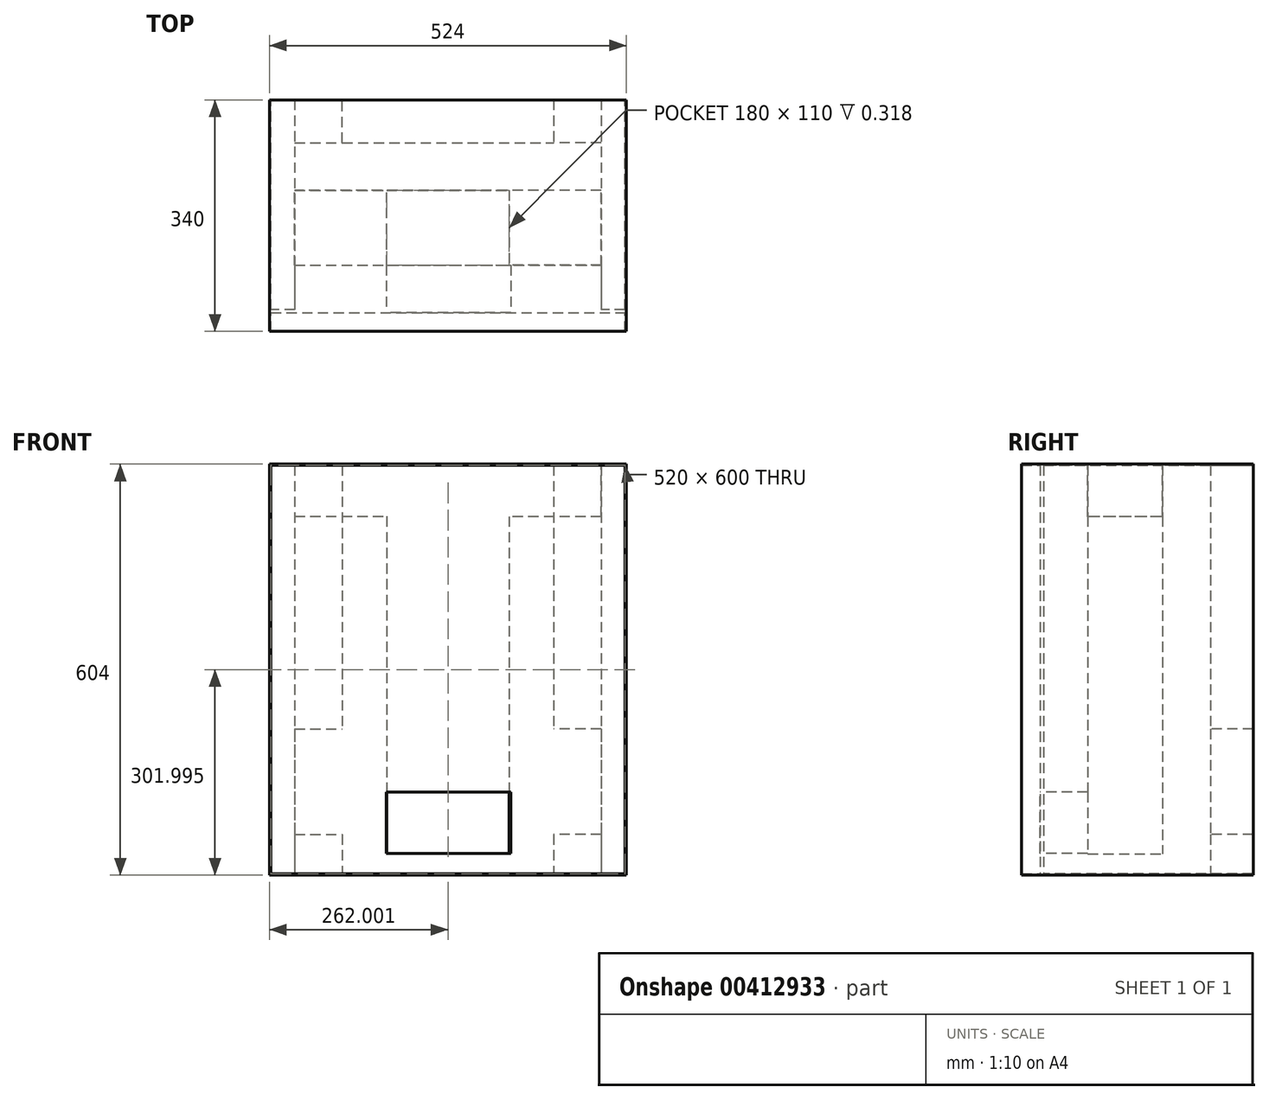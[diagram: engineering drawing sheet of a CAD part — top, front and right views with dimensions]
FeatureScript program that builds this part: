
annotation { "Feature Type Name" : "Feature", "Feature Type Description" : "" }
export const myFeature = defineFeature(function(context is Context, id is Id, definition is map)
    precondition{}
    {
        {
            var Q0;
            Q0=qCreatedBy(makeId("Front.planeOp"),FACE);
            var sketch = newSketch(context, id + "F0", { "sketchPlane" : qUnion([Q0])});
            skLineSegment(sketch, "E0.bottom", {"start": v(-23.65, 566.42) * mm, "end": v(500.35, 566.42) * mm});
            skLineSegment(sketch, "E0.top", {"start": v(-23.65, -37.58) * mm, "end": v(500.35, -37.58) * mm});
            skLineSegment(sketch, "E0.left", {"start": v(-23.65, 566.42) * mm, "end": v(-23.65, -37.58) * mm});
            skLineSegment(sketch, "E0.right", {"start": v(500.35, 566.42) * mm, "end": v(500.35, -37.58) * mm});
            skLineSegment(sketch, "E1.bottom", {"start": v(-21.65, 564.42) * mm, "end": v(498.35, 564.42) * mm});
            skLineSegment(sketch, "E1.top", {"start": v(-21.65, -35.58) * mm, "end": v(498.35, -35.58) * mm});
            skLineSegment(sketch, "E1.left", {"start": v(-21.65, 564.42) * mm, "end": v(-21.65, -35.58) * mm});
            skLineSegment(sketch, "E1.right", {"start": v(498.35, 564.42) * mm, "end": v(498.35, -35.58) * mm});
            skSolve(sketch);
        }
        {
            var Q0;
            Q0 = qSketchRegion(id + "F0", true);
            extrude(context, id + "F1", {"entities" : qUnion([Q0]), "depth" : 340 * mm});
        }
        {
            var Q0;
            Q0=makeQuery(id+"F1.opExtrude","SWEPT_FACE",FACE,{"disambiguationData":[OSD([sQuery(id+"F0.wireOp",EDGE,"E1.top")])]});
            var sketch = newSketch(context, id + "F2", { "sketchPlane" : qUnion([Q0])});
            skLineSegment(sketch, "E2", {"start": v(-21.65, -312.9) * mm, "end": v(498.35, -312.9) * mm});
            skLineSegment(sketch, "E3", {"start": v(498.35, -312.9) * mm, "end": v(498.35, -307.9) * mm});
            skLineSegment(sketch, "E4", {"start": v(498.35, -307.9) * mm, "end": v(-21.65, -307.9) * mm});
            skLineSegment(sketch, "E5", {"start": v(-21.65, -307.9) * mm, "end": v(-21.65, -312.9) * mm});
            skLineSegment(sketch, "E6", {"start": v(83.35, -307.9) * mm, "end": v(83.35, 0) * mm});
            skLineSegment(sketch, "E7", {"start": v(393.35, 0) * mm, "end": v(393.35, -307.9) * mm});
            skLineSegment(sketch, "E8", {"start": v(83.35, -67.9) * mm, "end": v(393.35, -67.9) * mm});
            skLineSegment(sketch, "E9", {"start": v(78.35, 0) * mm, "end": v(78.35, -307.9) * mm});
            skLineSegment(sketch, "E10", {"start": v(398.35, 0) * mm, "end": v(398.35, -307.9) * mm});
            skLineSegment(sketch, "E11", {"start": v(83.35, -62.9) * mm, "end": v(393.35, -62.9) * mm});
            skLineSegment(sketch, "E12", {"start": v(328.35, -132.9) * mm, "end": v(148.35, -132.9) * mm});
            skLineSegment(sketch, "E13", {"start": v(148.35, -132.9) * mm, "end": v(148.35, -242.9) * mm});
            skLineSegment(sketch, "E14", {"start": v(148.35, -242.9) * mm, "end": v(328.35, -242.9) * mm});
            skLineSegment(sketch, "E15", {"start": v(328.35, -242.9) * mm, "end": v(328.35, -132.9) * mm});
            skLineSegment(sketch, "E16", {"start": v(13.35, 0) * mm, "end": v(13.35, -307.9) * mm});
            skLineSegment(sketch, "E17", {"start": v(463.35, 0) * mm, "end": v(463.35, -307.9) * mm});
            skSolve(sketch);
        }
        {
            var Q0;
            Q0 = qSketchRegion(id + "F2", true);
            extrude(context, id + "F3", {"entities" : qUnion([Q0]), "operationType" : NewBodyOperationType.ADD, "depth" : 600 * mm});
        }
        {
            var Q0;
            {var subQ0=sQuery(id+"F2.wireOp",EDGE,"E9");Q0=makeQuery(id+"F2.imprint","IMPRINT",FACE,{"disambiguationData":[TD([[makeQuery(id+"F2.imprint","IMPRINT",EDGE,{"derivedFrom":subQ0}),-1.0]])]});}
            var Q1;
            {var subQ0=sQuery(id+"F2.wireOp",EDGE,"E10");Q1=makeQuery(id+"F2.imprint","IMPRINT",FACE,{"disambiguationData":[TD([[makeQuery(id+"F2.imprint","IMPRINT",EDGE,{"derivedFrom":subQ0}),1.0]])]});}
            extrude(context, id + "F4", {"entities" : qUnion([Q0, Q1]), "operationType" : NewBodyOperationType.ADD, "depth" : 600 * mm});
        }
        {
            var Q0;
            {var subQ4=sQuery(id+"F2.wireOp",EDGE,"E9");Q0=makeQuery(id+"F2.imprint","IMPRINT",FACE,{"disambiguationData":[TD([[makeQuery(id+"F2.imprint","IMPRINT",EDGE,{"derivedFrom":subQ4}),1.0]])]});}
            var Q1;
            {var subQ4=sQuery(id+"F2.wireOp",EDGE,"E10");Q1=makeQuery(id+"F2.imprint","IMPRINT",FACE,{"disambiguationData":[TD([[makeQuery(id+"F2.imprint","IMPRINT",EDGE,{"derivedFrom":subQ4}),-1.0]])]});}
            extrude(context, id + "F5", {"entities" : qUnion([Q0, Q1]), "operationType" : NewBodyOperationType.ADD, "depth" : 600 * mm});
        }
        {
            var Q0;
            Q0=makeQuery(id+"F3.opExtrude","SWEPT_FACE",FACE,{"disambiguationData":[OSD([sQuery(id+"F2.wireOp",EDGE,"E2")])]});
            var sketch = newSketch(context, id + "F6", { "sketchPlane" : qUnion([Q0])});
            skLineSegment(sketch, "E18", {"start": v(330.38, 84.42) * mm, "end": v(147.84, 84.42) * mm});
            skLineSegment(sketch, "E19", {"start": v(147.84, 84.42) * mm, "end": v(147.84, -5.58) * mm});
            skLineSegment(sketch, "E20", {"start": v(147.84, -5.58) * mm, "end": v(330.38, -5.58) * mm});
            skLineSegment(sketch, "E21", {"start": v(330.38, -5.58) * mm, "end": v(330.38, 84.42) * mm});
            skSolve(sketch);
        }
        {
            var Q0;
            Q0 = qSketchRegion(id + "F6", true);
            extrude(context, id + "F7", {"entities" : qUnion([Q0]), "operationType" : NewBodyOperationType.REMOVE, "oppositeDirection" : true, "depth" : 70 * mm});
        }
        {
            var Q0;
            Q0=makeQuery(id+"F3.opExtrude","SWEPT_FACE",FACE,{"disambiguationData":[OSD([sQuery(id+"F2.wireOp",EDGE,"E12")])]});
            var sketch = newSketch(context, id + "F8", { "sketchPlane" : qUnion([Q0])});
            skLineSegment(sketch, "E22.top", {"start": v(148.35, -35.58) * mm, "end": v(328.35, -35.58) * mm});
            skLineSegment(sketch, "E22.left", {"start": v(148.35, -5.9) * mm, "end": v(148.35, -35.58) * mm});
            skLineSegment(sketch, "E22.right", {"start": v(328.35, -5.9) * mm, "end": v(328.35, -35.58) * mm});
            skLineSegment(sketch, "E23", {"start": v(148.35, -5.9) * mm, "end": v(328.35, -5.9) * mm});
            skSolve(sketch);
        }
        {
            var Q0;
            Q0 = qSketchRegion(id + "F8", true);
            extrude(context, id + "F9", {"entities" : qUnion([Q0]), "operationType" : NewBodyOperationType.ADD, "depth" : 110 * mm});
        }
        {
            var Q0;
            Q0=makeQuery(id+"F5.opExtrude","SWEPT_FACE",FACE,{"disambiguationData":[OSD([sQuery(id+"F2.wireOp",EDGE,"E7")])]});
            var sketch = newSketch(context, id + "F10", { "sketchPlane" : qUnion([Q0])});
            skLineSegment(sketch, "E24.bottom", {"start": v(0, 22.26) * mm, "end": v(62.9, 22.26) * mm});
            skLineSegment(sketch, "E24.top", {"start": v(0, 177.26) * mm, "end": v(62.9, 177.26) * mm});
            skLineSegment(sketch, "E24.left", {"start": v(0, 22.26) * mm, "end": v(0, 177.26) * mm});
            skLineSegment(sketch, "E24.right", {"start": v(62.9, 22.26) * mm, "end": v(62.9, 177.26) * mm});
            skSolve(sketch);
        }
        {
            var Q0;
            Q0 = qSketchRegion(id + "F10", true);
            extrude(context, id + "F11", {"entities" : qUnion([Q0]), "operationType" : NewBodyOperationType.REMOVE, "oppositeDirection" : true, "depth" : 70 * mm});
        }
        {
            var Q0;
            Q0=makeQuery(id+"F10.imprint","IMPRINT",FACE,{"disambiguationData":[TD([[makeQuery(id+"F10.imprint","IMPRINT",EDGE,{"derivedFrom":sQuery(id+"F10.wireOp",EDGE,"E24.bottom")}),1.0]])]});
            extrude(context, id + "F12", {"entities" : qUnion([Q0]), "operationType" : NewBodyOperationType.REMOVE, "depth" : 380 * mm});
        }
        {
            var Q0;
            Q0=makeQuery(id+"F3.opExtrude","SWEPT_FACE",FACE,{"disambiguationData":[OSD([sQuery(id+"F2.wireOp",EDGE,"E13")])]});
            var sketch = newSketch(context, id + "F13", { "sketchPlane" : qUnion([Q0])});
            skLineSegment(sketch, "E25.bottom", {"start": v(-242.9, 564.42) * mm, "end": v(-132.9, 564.42) * mm});
            skLineSegment(sketch, "E25.top", {"start": v(-242.9, 489.42) * mm, "end": v(-132.9, 489.42) * mm});
            skLineSegment(sketch, "E25.left", {"start": v(-242.9, 564.42) * mm, "end": v(-242.9, 489.42) * mm});
            skLineSegment(sketch, "E25.right", {"start": v(-132.9, 564.42) * mm, "end": v(-132.9, 489.42) * mm});
            skSolve(sketch);
        }
        {
            var Q0;
            Q0 = qSketchRegion(id + "F13", true);
            extrude(context, id + "F14", {"entities" : qUnion([Q0]), "operationType" : NewBodyOperationType.REMOVE, "oppositeDirection" : true, "depth" : 140 * mm});
        }
        {
            var Q0;
            Q0=makeQuery(id+"F3.opExtrude","SWEPT_FACE",FACE,{"disambiguationData":[OSD([sQuery(id+"F2.wireOp",EDGE,"E15")])]});
            var sketch = newSketch(context, id + "F15", { "sketchPlane" : qUnion([Q0])});
            skLineSegment(sketch, "E26.bottom", {"start": v(132.9, 564.42) * mm, "end": v(242.9, 564.42) * mm});
            skLineSegment(sketch, "E26.top", {"start": v(132.9, 489.3) * mm, "end": v(242.9, 489.3) * mm});
            skLineSegment(sketch, "E26.left", {"start": v(132.9, 564.42) * mm, "end": v(132.9, 489.3) * mm});
            skLineSegment(sketch, "E26.right", {"start": v(242.9, 564.42) * mm, "end": v(242.9, 489.3) * mm});
            skSolve(sketch);
        }
        {
            var Q0;
            Q0 = qSketchRegion(id + "F15", true);
            extrude(context, id + "F16", {"entities" : qUnion([Q0]), "operationType" : NewBodyOperationType.REMOVE, "oppositeDirection" : true, "depth" : 140 * mm});
        }
    });
